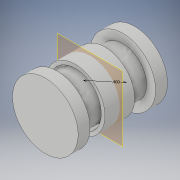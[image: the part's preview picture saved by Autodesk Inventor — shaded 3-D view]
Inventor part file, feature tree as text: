
AUTODESK INVENTOR PART (.ipt)
format: ipt  version: 2018 (Build 220112000, 112)  size: 133,632 bytes
history: native  units: in
note: dims shown in document units (in); Inventor stores cm internally (conversion verified against a paired STEP export)
features: extrude x4, sketch x3, plane x2, mirror x1
ambient origin geometry x8: Origin, YZ Plane, XZ Plane, XY Plane, X Axis, Y Axis, Z Axis, Center Point
bodies: Solid1 (feature_tree)
feature tree (10):
  sketch  "Sketch1"  dims[d0=0.4in d1=0.4in d2=0.0in]
  extrude  "Extrusion1"  Depth=0.4in TaperAngle=0.0deg
  plane  "Work Plane1"
  extrude  "Extrusion4"  Depth=0.5in
  extrude  "Extrusion5"  Depth=0.15in TaperAngle=0.0deg
  extrude  "Extrusion6"  Depth=0.1in TaperAngle=0.0deg
  plane  "Work Plane2"
  mirror  "Mirror2"
  sketch  "Sketch4"  dims[d13=0.44in d14=0.5in]
  sketch  "Sketch5"  dims[d15=0.25in d16=0.0in d17=0.15in d18=0.0in d23=0.1in d24=0.0in d25=0.55in]
